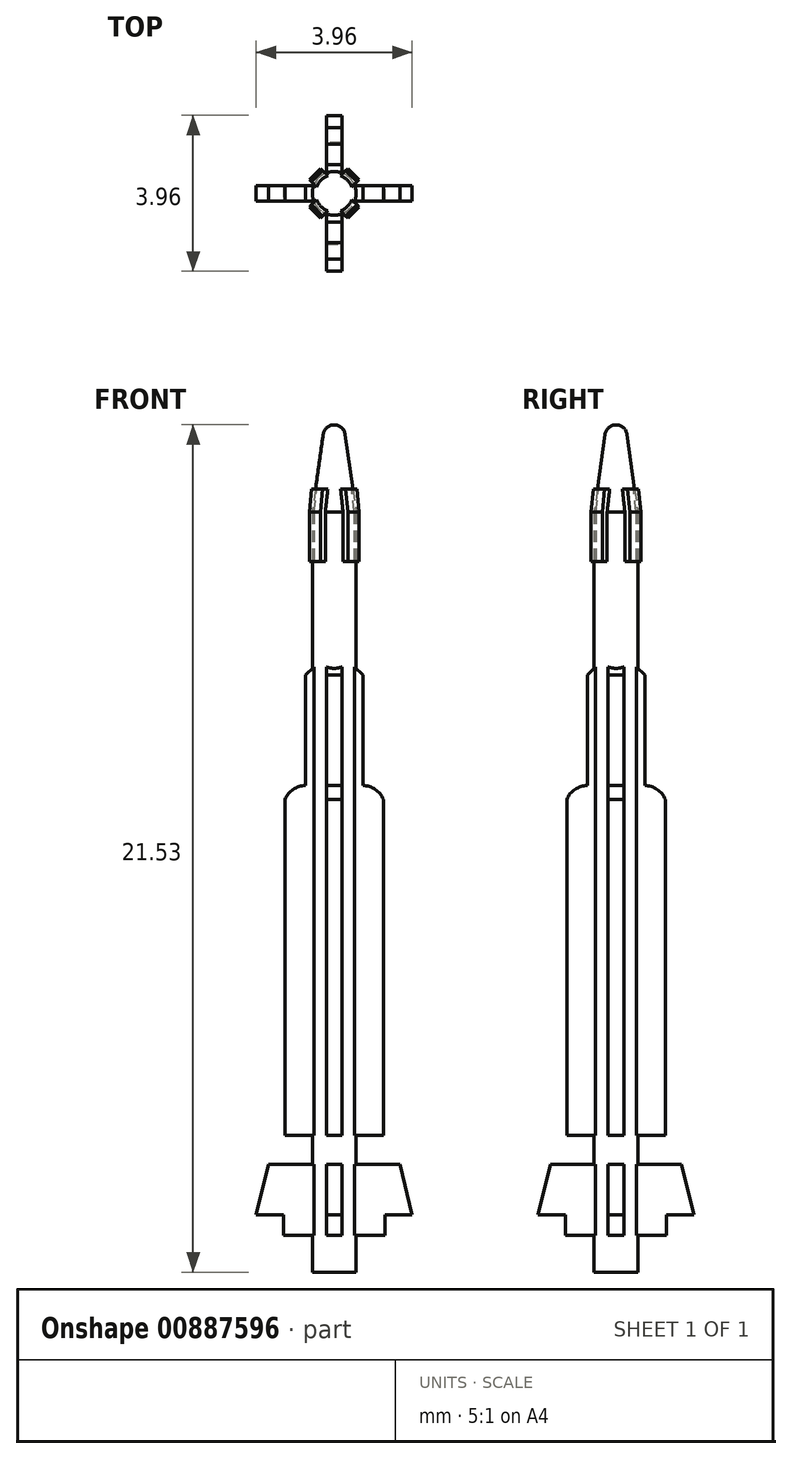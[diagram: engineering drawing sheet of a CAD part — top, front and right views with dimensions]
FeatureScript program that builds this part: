
annotation { "Feature Type Name" : "Feature", "Feature Type Description" : "" }
export const myFeature = defineFeature(function(context is Context, id is Id, definition is map)
    precondition{}
    {
        {
            var Q0;
            Q0=qCreatedBy(makeId("Front.planeOp"),FACE);
            var sketch = newSketch(context, id + "F0", { "sketchPlane" : qUnion([Q0])});
            skLineSegment(sketch, "E0", {"start": v(0, 0) * mm, "end": v(0, 21.53) * mm});
            skLineSegment(sketch, "E1", {"start": v(0.56, 19.3) * mm, "end": v(0.56, 0) * mm});
            skLineSegment(sketch, "E2", {"start": v(0.56, 0) * mm, "end": v(0, 0) * mm});
            skArc(sketch, "E3", {"start": v(0.28, 21.28) * mm, "mid": v(0.19, 21.46) * mm, "end": v(0, 21.53) * mm});
            skLineSegment(sketch, "E4", {"start": v(0.28, 21.28) * mm, "end": v(0.56, 19.3) * mm});
            skSolve(sketch);
        }
        {
            var Q0;
            {var subQ0=sQuery(id+"F0.wireOp",EDGE,"mrwio9nY-PsAZ-Zbfy-NhIU-sYq0QVbgGXAG");Q0=makeQuery(id+"F0.imprint","IMPRINT",FACE,{"disambiguationData":[TD([[makeQuery(id+"F0.imprint","IMPRINT",EDGE,{"derivedFrom":subQ0}),-1.0]])]});}
            var Q1;
            Q1=makeQuery(id+"F0.imprint","IMPRINT",FACE,{"disambiguationData":[TD([[makeQuery(id+"F0.imprint","IMPRINT",EDGE,{"derivedFrom":sQuery(id+"F0.wireOp",EDGE,"rEedh4zr-IGRr-Hqzj-sDLB-QnI7VE1V64O6.bottom")}),-1.0]])]});
            var Q2;
            Q2=makeQuery(id+"F0.imprint","IMPRINT",FACE,{"disambiguationData":[TD([[makeQuery(id+"F0.imprint","IMPRINT",EDGE,{"derivedFrom":sQuery(id+"F0.wireOp",EDGE,"E0")}),-1.0]])]});
            var Q3;
            Q3=makeQuery(id+"F0.imprint","IMPRINT",FACE,{"disambiguationData":[TD([[makeQuery(id+"F0.imprint","IMPRINT",EDGE,{"derivedFrom":sQuery(id+"F0.wireOp",EDGE,"p5wuz8j9-3HT4-kWwn-DjtP-lJmqTNSXSBJY.bottom")}),-1.0]])]});
            var Q4;
            Q4=sQuery(id+"F0.wireOp",EDGE,"E0");
            revolve(context, id + "F1", {"surfaceOperationType" : NewSurfaceOperationType.NEW, "entities" : qUnion([Q0, Q1, Q2, Q3]), "axis" : qUnion([Q4]), "revolveType" : RevolveType.FULL});
        }
        {
            var Q0;
            Q0=qCreatedBy(makeId("Front.planeOp"),FACE);
            var sketch = newSketch(context, id + "F2", { "sketchPlane" : qUnion([Q0])});
            skLineSegment(sketch, "E5", {"start": v(0, 0) * mm, "end": v(0, 16.56) * mm});
            skLineSegment(sketch, "E6", {"start": v(0, 2.74) * mm, "end": v(1.67, 2.74) * mm});
            skLineSegment(sketch, "E7", {"start": v(0.56, 0) * mm, "end": v(0.56, 32.87) * mm, "construction": true});
            skLineSegment(sketch, "E8", {"start": v(1.28, 0.94) * mm, "end": v(0, 0.94) * mm});
            skLineSegment(sketch, "E9", {"start": v(1.28, 0.94) * mm, "end": v(1.28, 1.46) * mm});
            skLineSegment(sketch, "E10", {"start": v(1.28, 1.46) * mm, "end": v(1.98, 1.46) * mm});
            skLineSegment(sketch, "E11", {"start": v(1.98, 1.46) * mm, "end": v(1.67, 2.74) * mm});
            skLineSegment(sketch, "E12", {"start": v(0, 3.47) * mm, "end": v(1.25, 3.47) * mm});
            skLineSegment(sketch, "E13", {"start": v(1.25, 3.47) * mm, "end": v(1.25, 12.01) * mm});
            skLineSegment(sketch, "E14.0", {"start": v(0.56, 0) * mm, "end": v(-0.56, 0) * mm});
            skArc(sketch, "E15", {"start": v(1.25, 12.01) * mm, "mid": v(1.04, 12.27) * mm, "end": v(0.73, 12.36) * mm});
            skLineSegment(sketch, "E16", {"start": v(0.73, 12.36) * mm, "end": v(0.73, 15.42) * mm});
            skLineSegment(sketch, "E17", {"start": v(0.73, 15.42) * mm, "end": v(0, 15.42) * mm});
            skSolve(sketch);
        }
        {
            var Q0;
            Q0=qSketchRegion(id+"F2",true);
            extrude(context, id + "F3", {"entities" : qUnion([Q0]), "operationType" : NewBodyOperationType.ADD, "depth" : .4 * mm, "offsetDistance" : 25 * mm, "symmetric" : true});
        }
        {
            var Q0;
            Q0=qCreatedBy(makeId("Front.planeOp"),FACE);
            var Q1;
            Q1=qCreatedBy(makeId("Right.planeOp"),FACE);
            cPlane(context, id + "F4", {"entities" : qUnion([Q0, Q1]), "cplaneType" : CPlaneType.MID_PLANE, "offset" : 25 * mm, "width" : 150 * mm, "height" : 150 * mm});
        }
        {
            var Q0;
            Q0=qCreatedBy(id+"F4.planeOp",FACE);
            var sketch = newSketch(context, id + "F5", { "sketchPlane" : qUnion([Q0])});
            skLineSegment(sketch, "E18", {"start": v(0, 18.06) * mm, "end": v(0.7, 18.06) * mm});
            skLineSegment(sketch, "E19", {"start": v(0.7, 18.06) * mm, "end": v(0.7, 19.3) * mm});
            skLineSegment(sketch, "E20", {"start": v(0.61, 19.9) * mm, "end": v(0, 19.9) * mm});
            skLineSegment(sketch, "E21", {"start": v(0, 19.9) * mm, "end": v(0, 18.06) * mm});
            skLineSegment(sketch, "E22.0", {"start": v(0.56, 19.3) * mm, "end": v(-0.56, 19.3) * mm});
            skLineSegment(sketch, "E23", {"start": v(0.56, 19.3) * mm, "end": v(0.56, 17.15) * mm, "construction": true});
            skLineSegment(sketch, "E24", {"start": v(0.7, 19.3) * mm, "end": v(0.61, 19.9) * mm});
            skLineSegment(sketch, "E25.0", {"start": v(0.28, 21.28) * mm, "end": v(-0.28, 21.28) * mm});
            skLineSegment(sketch, "E26", {"start": v(0.28, 21.28) * mm, "end": v(0.56, 19.3) * mm, "construction": true});
            skSolve(sketch);
        }
        {
            var Q0;
            Q0=qSketchRegion(id+"F5",true);
            extrude(context, id + "F6", {"entities" : qUnion([Q0]), "operationType" : NewBodyOperationType.ADD, "depth" : .4 * mm, "offsetDistance" : 25 * mm, "symmetric" : true});
        }
        {
            var Q0;
            Q0=makeQuery(id+"F1.opRevolve","SWEPT_BODY",BODY,{"disambiguationData":[OSD([sQuery(id+"F0.wireOp",EDGE,"E0"),sQuery(id+"F0.wireOp",EDGE,"E1"),sQuery(id+"F0.wireOp",EDGE,"E2"),sQuery(id+"F0.wireOp",EDGE,"2EiOItwe-9FNA-eY8p-DkXH-AMy5AHyUmzZA"),sQuery(id+"F0.wireOp",EDGE,"lF35QjYl-MEgV-fRWE-0Yr6-Bt5vS8A7brRf")])]});
            var Q1;
            Q1=makeQuery(id+"F1.opRevolve","SWEPT_FACE",FACE,{"disambiguationData":[OSD([sQuery(id+"F0.wireOp",EDGE,"E1")])]});
            circularPattern(context, id + "F7", {"operationType" : NewBodyOperationType.ADD, "entities" : qUnion([Q0]), "axis" : qUnion([Q1]), "angle" : 360 * degree, "instanceCount" : 4, "equalSpace" : true, "computeTransformsWithoutBuiltin" : true});
        }
        {
            var Q0;
            Q0=makeQuery(id+"F7.opPattern","COPY",EDGE,{"derivedFrom":makeQuery(id+"F3.opExtrude","SWEPT_EDGE",EDGE,{"disambiguationData":[OSD([sQuery(id+"F2.wireOp",EDGE,"E16"),sQuery(id+"F2.wireOp",EDGE,"E17")])]}),"instanceName":"2"});
            var Q1;
            Q1=makeQuery(id+"F7.opPattern","COPY",EDGE,{"derivedFrom":makeQuery(id+"F3.opExtrude","SWEPT_EDGE",EDGE,{"disambiguationData":[OSD([sQuery(id+"F2.wireOp",EDGE,"E16"),sQuery(id+"F2.wireOp",EDGE,"E17")])]}),"instanceName":"3"});
            var Q2;
            Q2=makeQuery(id+"F3.opExtrude","SWEPT_EDGE",EDGE,{"disambiguationData":[OSD([sQuery(id+"F2.wireOp",EDGE,"E16"),sQuery(id+"F2.wireOp",EDGE,"E17")])]});
            var Q3;
            Q3=makeQuery(id+"F7.opPattern","COPY",EDGE,{"derivedFrom":makeQuery(id+"F3.opExtrude","SWEPT_EDGE",EDGE,{"disambiguationData":[OSD([sQuery(id+"F2.wireOp",EDGE,"E16"),sQuery(id+"F2.wireOp",EDGE,"E17")])]}),"instanceName":"1"});
            chamfer(context, id + "F8", {"entities" : qUnion([Q0, Q1, Q2, Q3]), "width" : .25 * mm, "tangentPropagation" : true});
        }
    });
